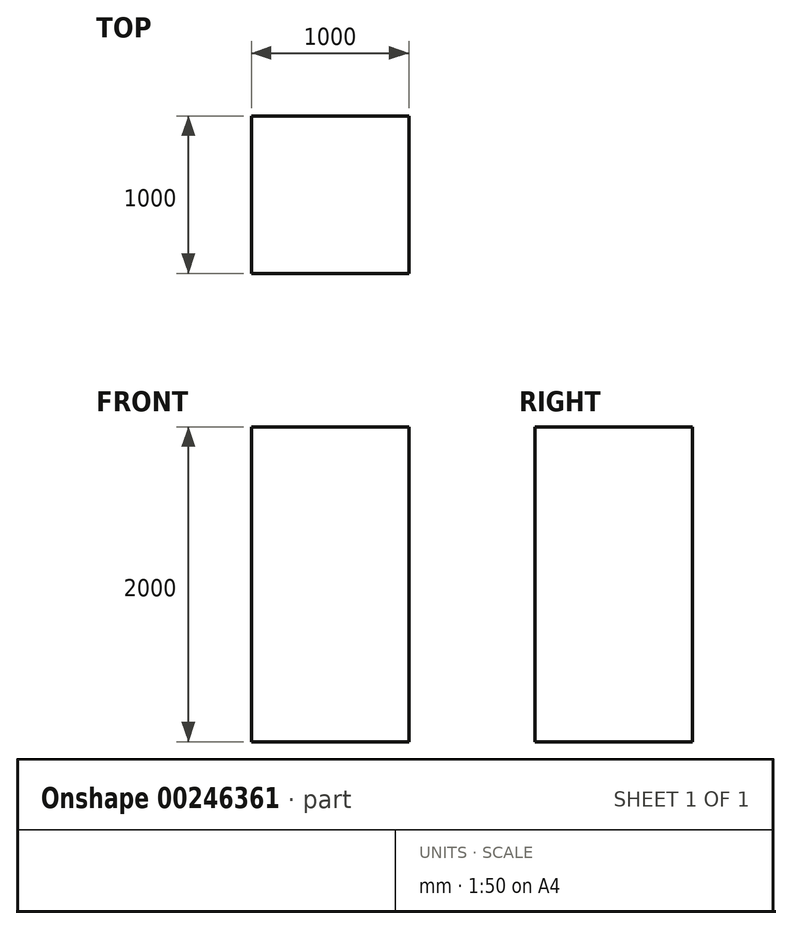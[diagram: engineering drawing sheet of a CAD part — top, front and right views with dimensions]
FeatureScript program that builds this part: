
annotation { "Feature Type Name" : "Feature", "Feature Type Description" : "" }
export const myFeature = defineFeature(function(context is Context, id is Id, definition is map)
    precondition{}
    {
        {
            var Q0;
            Q0=qCreatedBy(makeId("Front.planeOp"),FACE);
            var sketch = newSketch(context, id + "F0", { "sketchPlane" : qUnion([Q0])});
            skLineSegment(sketch, "E0.bottom", {"start": v(-500, 1000) * mm, "end": v(500, 1000) * mm});
            skLineSegment(sketch, "E0.top", {"start": v(-500, -1000) * mm, "end": v(500, -1000) * mm});
            skLineSegment(sketch, "E0.left", {"start": v(-500, 1000) * mm, "end": v(-500, -1000) * mm});
            skLineSegment(sketch, "E0.right", {"start": v(500, 1000) * mm, "end": v(500, -1000) * mm});
            skPoint(sketch, "E0.middle", {"position": v(0, 0) * mm});
            skSolve(sketch);
        }
        {
            var Q0;
            Q0 = qSketchRegion(id + "F0", true);
            extrude(context, id + "F1", {"entities" : qUnion([Q0]), "endBound" : BoundingType.SYMMETRIC, "depth" : 1000 * mm});
        }
    });
